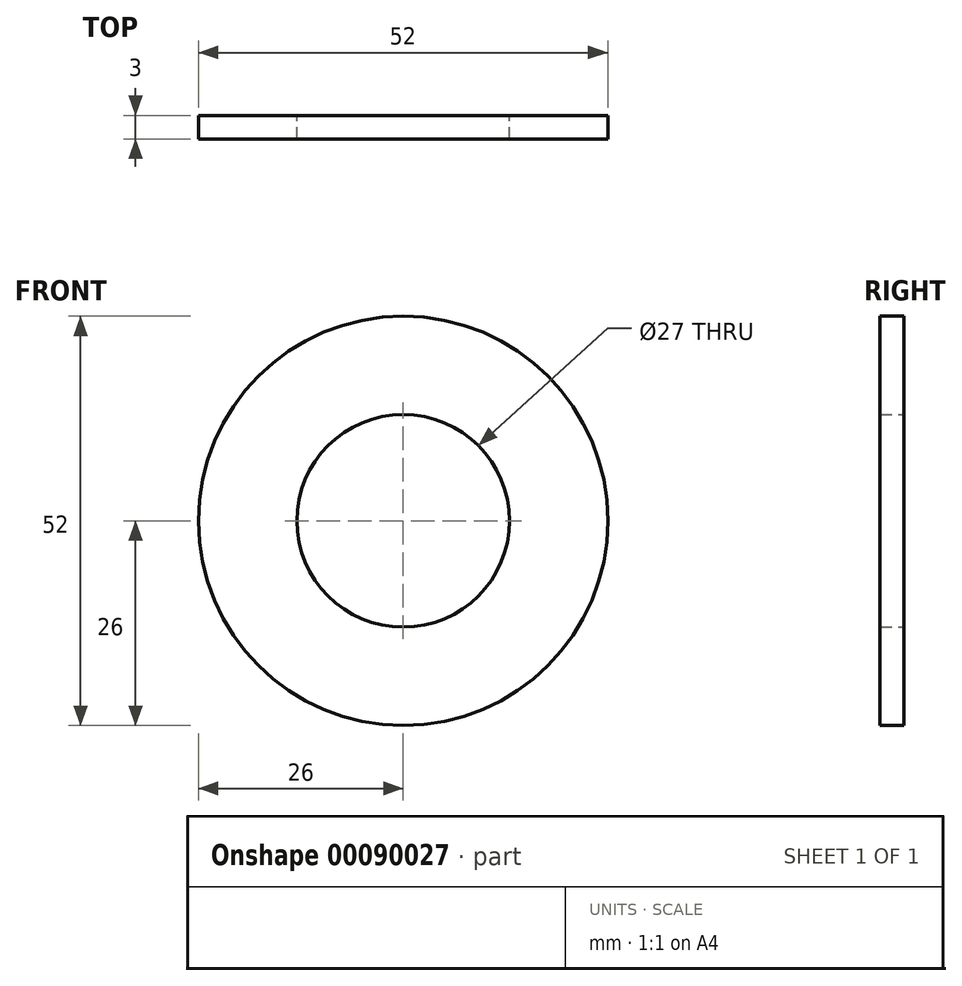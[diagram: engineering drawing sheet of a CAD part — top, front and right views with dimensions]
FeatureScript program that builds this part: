
annotation { "Feature Type Name" : "Feature", "Feature Type Description" : "" }
export const myFeature = defineFeature(function(context is Context, id is Id, definition is map)
    precondition{}
    {
        {
            var Q0;
            Q0=qCreatedBy(makeId("Front.planeOp"),FACE);
            var sketch = newSketch(context, id + "F0", { "sketchPlane" : qUnion([Q0])});
            skCircle(sketch, "E0", {"center": v(0, 0) * mm, "radius": 26 * mm});
            skCircle(sketch, "E1", {"center": v(0, 0) * mm, "radius": 13.5 * mm});
            skSolve(sketch);
        }
        {
            var Q0;
            Q0=makeQuery(id+"F0.imprint","IMPRINT",FACE,{"disambiguationData":[TD([[makeQuery(id+"F0.imprint","IMPRINT",EDGE,{"derivedFrom":sQuery(id+"F0.wireOp",EDGE,"E0")}),1.0]])]});
            extrude(context, id + "F1", {"entities" : qUnion([Q0]), "depth" : 3 * mm, "symmetric" : true});
        }
    });
